# Revit family: Franke_Under_table_refrigerator_UT05_EC-A600_MS_EC_A600_FM_EC_A800_FM_EC(CN)
name_source: partatom
category: Specialty Equipment
revit_build: Autodesk Revit 2015 (Build: 20140606_1530(x64)
units: mm (PartAtom-declared; Revit-internal decimal feet)

## types (1)
- Under table refrigerator UT05 EC-A600 MS EC,A600 FM EC,A800 FM EC(220V/CN)
    Assembly Code = key module Under table refrigerator UT05
    Cost = 0 $
    Current consumption = 1 A
    Cycle = 50 Hz
    Cycle Alternative = 0 Hz
    Depth (mm) = 475 mm  [stored 1.5584 ft]
    Description = key module Under table refrigerator UT05 for storage of cooled milk
    Energy loss acc. to DIN 18873 = 0.638 kWh/24 h - 230 V
    Height (mm) = 544 mm  [stored 1.78478 ft]
    Keynote = key module Under table refrigerator UT05
    Manufacturer = Franke
    Max Overcurrent Protection = -
    Milk storage = 5 l
    Model = 410879 - Under table refrigerator UT05 EC - A600 MS EC, A600 FM EC, A800 FM EC
    Number of Nutral Conductors = 1
    Number of Poles = 1
    Number of Protective Conductors = 1
    Temperature range = + 3° to + 8°
    URL = https://www.franke.com
    Volts max. = 0 V
    Volts min. = 220 V
    Weight = 18 kg
    Width (mm) = 270 mm  [stored 0.885827 ft]

note: [stored X ft] marks values corroborated as IEEE doubles in the binary element streams (Revit-internal decimal feet)
